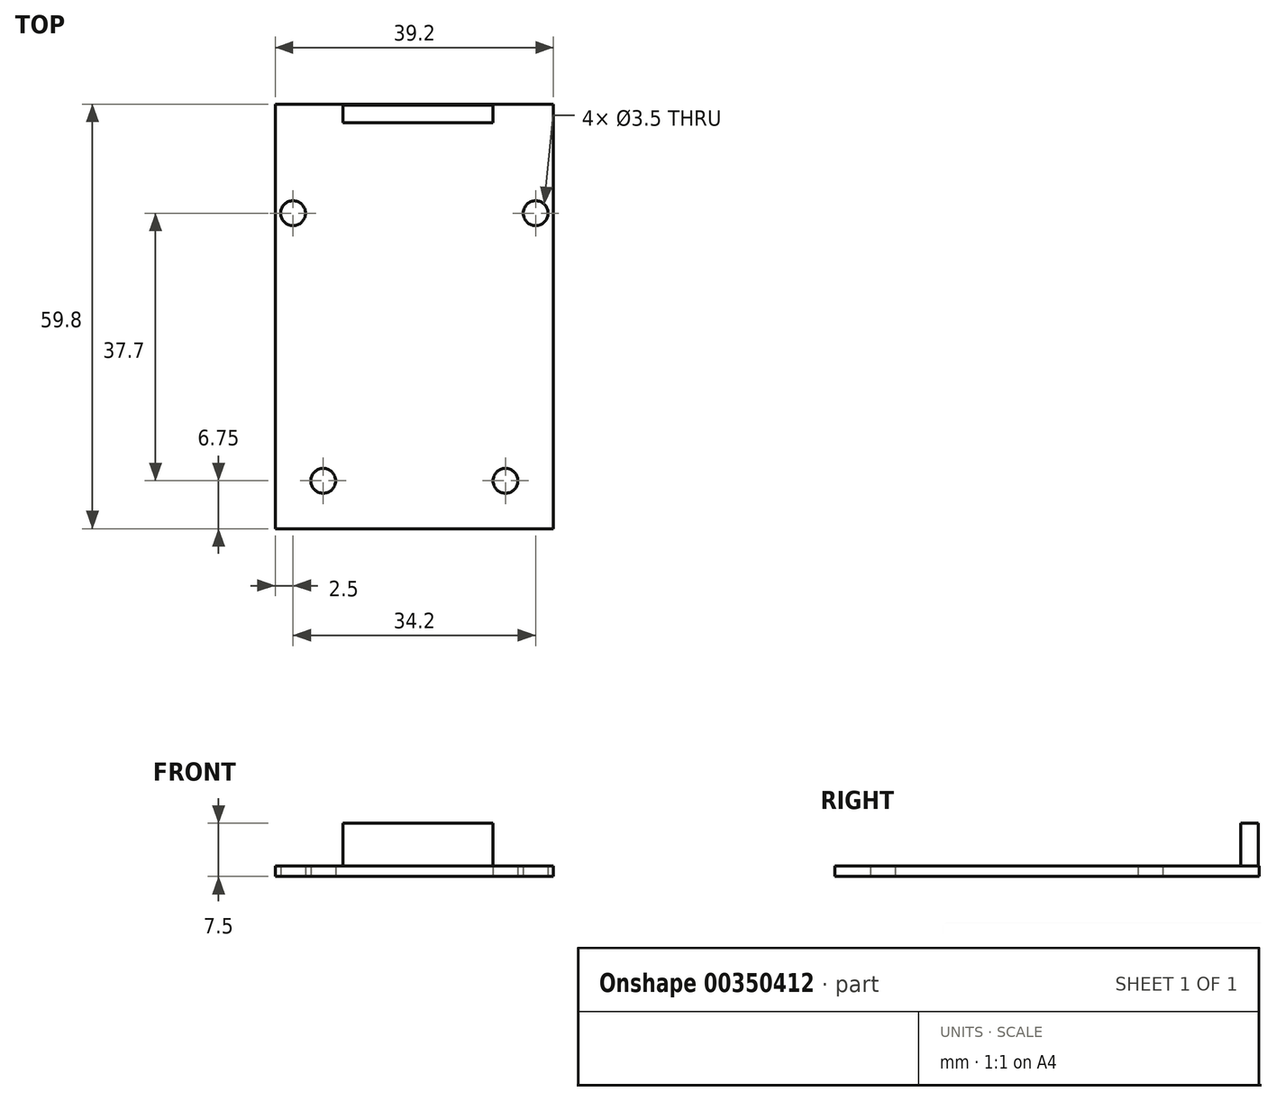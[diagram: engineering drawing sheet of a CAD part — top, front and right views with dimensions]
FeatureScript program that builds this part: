
annotation { "Feature Type Name" : "Feature", "Feature Type Description" : "" }
export const myFeature = defineFeature(function(context is Context, id is Id, definition is map)
    precondition{}
    {
        {
            var Q0;
            Q0=qCreatedBy(makeId("Top.planeOp"),FACE);
            var sketch = newSketch(context, id + "F0", { "sketchPlane" : qUnion([Q0])});
            skLineSegment(sketch, "E0.bottom", {"start": v(19.6, -29.9) * mm, "end": v(-19.6, -29.9) * mm});
            skLineSegment(sketch, "E0.top", {"start": v(19.6, 29.9) * mm, "end": v(-19.6, 29.9) * mm});
            skLineSegment(sketch, "E0.left", {"start": v(19.6, -29.9) * mm, "end": v(19.6, 29.9) * mm});
            skLineSegment(sketch, "E0.right", {"start": v(-19.6, -29.9) * mm, "end": v(-19.6, 29.9) * mm});
            skPoint(sketch, "E0.middle", {"position": v(0, 0) * mm});
            skCircle(sketch, "E1", {"center": v(-17.1, 14.55) * mm, "radius": 1.75 * mm});
            skCircle(sketch, "E2", {"center": v(17.1, 14.55) * mm, "radius": 1.75 * mm});
            skCircle(sketch, "E3", {"center": v(-12.85, -23.15) * mm, "radius": 1.75 * mm});
            skCircle(sketch, "E4", {"center": v(12.85, -23.15) * mm, "radius": 1.75 * mm});
            skSolve(sketch);
        }
        {
            var Q0;
            Q0 = qSketchRegion(id + "F0", true);
            extrude(context, id + "F1", {"entities" : qUnion([Q0]), "depth" : 1.5 * mm});
        }
        {
            var Q0;
            Q0=makeQuery(id+"F1.opExtrude","CAP_FACE",FACE,{"disambiguationData":[OSD([sQuery(id+"F0.wireOp",EDGE,"E0.bottom"),sQuery(id+"F0.wireOp",EDGE,"E0.top"),sQuery(id+"F0.wireOp",EDGE,"E0.left"),sQuery(id+"F0.wireOp",EDGE,"E0.right"),sQuery(id+"F0.wireOp",EDGE,"E1"),sQuery(id+"F0.wireOp",EDGE,"E2"),sQuery(id+"F0.wireOp",EDGE,"E3"),sQuery(id+"F0.wireOp",EDGE,"E4")])],"isStart":false});
            var sketch = newSketch(context, id + "F2", { "sketchPlane" : qUnion([Q0])});
            skLineSegment(sketch, "E5.bottom", {"start": v(-10.1, 29.8) * mm, "end": v(11.1, 29.8) * mm});
            skLineSegment(sketch, "E5.top", {"start": v(-10.1, 27.3) * mm, "end": v(11.1, 27.3) * mm});
            skLineSegment(sketch, "E5.left", {"start": v(-10.1, 29.8) * mm, "end": v(-10.1, 27.3) * mm});
            skLineSegment(sketch, "E5.right", {"start": v(11.1, 29.8) * mm, "end": v(11.1, 27.3) * mm});
            skSolve(sketch);
        }
        {
            var Q0;
            Q0 = qSketchRegion(id + "F2", true);
            extrude(context, id + "F3", {"entities" : qUnion([Q0]), "operationType" : NewBodyOperationType.ADD, "depth" : 6 * mm});
        }
    });
